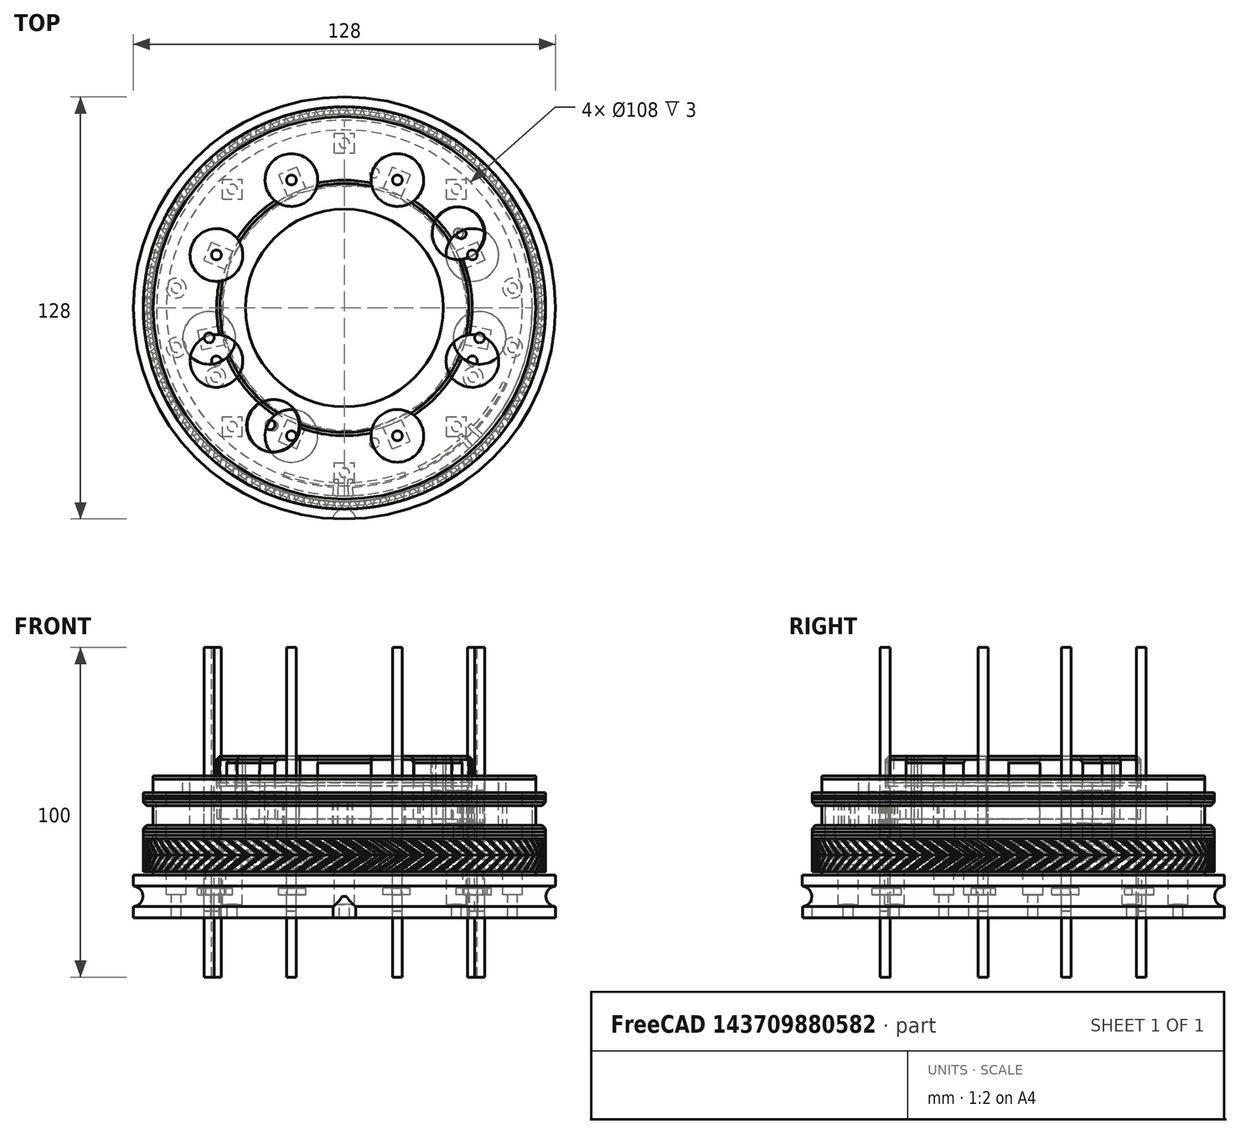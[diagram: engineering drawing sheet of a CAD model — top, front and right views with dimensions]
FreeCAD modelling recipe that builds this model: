
FCSTD DOCUMENT  (FreeCAD 0.19R24276 (Git))
Label: bazovina-part-F_pedestal_028
License: All rights reserved
LicenseURL: http://en.wikipedia.org/wiki/All_rights_reserved
objects: Part::Cylinder×215, Part::Cut×53, Part::Compound×50, Part::Box×36, Part::FeaturePython×26, Part::Chamfer×6, Mesh::Feature×4, Part::Torus×1
note: 387 computed .brp shape members not serialized (recipe doc carries the construction recipe); baked Part::Feature solids carry a one-line shape summary decoded from their .brp

FEATURE [Part::FeaturePython] Tube022  # WARN: FeaturePython — macro-defined, semantics opaque (R4)
  AttacherType = Attacher::AttachEngine3D
  Height = 19
  InnerRadius = 30
  OuterRadius = 58
  Placement = pos=(0,0,42) rot=(0,0,1;0rad)
FEATURE [Part::Cylinder] Cylinder433  label="Válec433"
  Angle = 360
  AttacherType = Attacher::AttachEngine3D
  Height = 18
  Placement = pos=(34.6278,22.6371,43.6023) rot=(-0.009819,-0.0017,0.99995;2.52972rad)
  Radius = 8
FEATURE [Part::Cylinder] Cylinder434  label="Válec434"
  Angle = 360
  AttacherType = Attacher::AttachEngine3D
  Height = 100
  Placement = pos=(16.0727,38.8029,0) rot=(0,0,1;3.14159rad)
  Radius = 1.5
FEATURE [Part::Cylinder] Cylinder435  label="Válec435"
  Angle = 360
  AttacherType = Attacher::AttachEngine3D
  Height = 18
  Placement = pos=(16.0725,38.7989,43) rot=(0,0,1;3.14159rad)
  Radius = 8
FEATURE [Part::Cylinder] Cylinder430  label="Válec430"
  Angle = 360
  AttacherType = Attacher::AttachEngine3D
  Height = 100
  Placement = pos=(38.8029,-16.0727,0) rot=(0,0,1;1.5708rad)
  Radius = 1.5
FEATURE [Part::Cylinder] Cylinder428  label="Válec428"
  Angle = 360
  AttacherType = Attacher::AttachEngine3D
  Height = 100
  Placement = pos=(16.0727,-38.8029,0) rot=(0,0,1;0.785398rad)
  Radius = 1.5
FEATURE [Part::Cylinder] Cylinder429  label="Válec429"
  Angle = 360
  AttacherType = Attacher::AttachEngine3D
  Height = 18
  Placement = pos=(16.07,-38.8,43) rot=(0,0,1;0.785398rad)
  Radius = 8
FEATURE [Part::Cylinder] Cylinder432  label="Válec432"
  Angle = 360
  AttacherType = Attacher::AttachEngine3D
  Height = 100
  Placement = pos=(35.44,22.5307,0.610113) rot=(-0.009819,-0.0017,0.99995;2.52972rad)
  Radius = 1.5
FEATURE [Part::Cylinder] Cylinder436  label="Válec436"
  Angle = 360
  AttacherType = Attacher::AttachEngine3D
  Height = 100
  Placement = pos=(-16.0727,38.8029,0) rot=(0,0,1;3.92699rad)
  Radius = 1.5
FEATURE [Part::Cylinder] Cylinder431  label="Válec431"
  Angle = 360
  AttacherType = Attacher::AttachEngine3D
  Height = 18
  Placement = pos=(38.7989,-16.0725,43) rot=(0,0,1;1.5708rad)
  Radius = 8
FEATURE [Part::Cylinder] Cylinder443  label="Válec443"
  Angle = 360
  AttacherType = Attacher::AttachEngine3D
  Height = 18
  Placement = pos=(-21.7485,-35.6902,43.196) rot=(0.02393,0.106372,-0.994038;0.174533rad)
  Radius = 8
FEATURE [Part::Cylinder] Cylinder438  label="Válec438"
  Angle = 360
  AttacherType = Attacher::AttachEngine3D
  Height = 100
  Placement = pos=(-38.8029,16.0727,0) rot=(0,0,-1;1.5708rad)
  Radius = 1.5
FEATURE [Part::Cylinder] Cylinder441  label="Válec441"
  Angle = 360
  AttacherType = Attacher::AttachEngine3D
  Height = 18
  Placement = pos=(-38.8,-16.07,43) rot=(0,0,-1;0.785398rad)
  Radius = 8
FEATURE [Part::Cylinder] Cylinder440  label="Válec440"
  Angle = 360
  AttacherType = Attacher::AttachEngine3D
  Height = 100
  Placement = pos=(-38.8029,-16.0727,0) rot=(0,0,-1;0.785398rad)
  Radius = 1.5
FEATURE [Part::Cylinder] Cylinder439  label="Válec439"
  Angle = 360
  AttacherType = Attacher::AttachEngine3D
  Height = 18
  Placement = pos=(-38.7989,16.0725,43) rot=(0,0,-1;1.5708rad)
  Radius = 8
FEATURE [Part::Cylinder] Cylinder442  label="Válec442"
  Angle = 360
  AttacherType = Attacher::AttachEngine3D
  Height = 100
  Placement = pos=(-22.5281,-35.4464,0.203785) rot=(0.02393,0.106372,-0.994038;0.174533rad)
  Radius = 1.5
FEATURE [Part::Compound] Compound321
  Links = -> [Cylinder428,Cylinder430,Cylinder432,Cylinder434,Cylinder436,Cylinder438,Cylinder440,Cylinder442]
FEATURE [Part::Cylinder] Cylinder437  label="Válec437"
  Angle = 360
  AttacherType = Attacher::AttachEngine3D
  Height = 18
  Placement = pos=(-16.07,38.8,43) rot=(0,0,1;3.92699rad)
  Radius = 8
FEATURE [Part::Compound] Compound323
  Links = -> [Cylinder441,Cylinder439,Cylinder437,Cylinder435,Cylinder433,Cylinder431,Cylinder429,Cylinder443]
  Placement = pos=(0,0,3) rot=(0,0,1;0rad)
FEATURE [Part::Cut] Cut169
  Base = -> Tube022
  Tool = -> Compound323
FEATURE [Part::Compound] Compound324
  Links = -> [Cut169]
FEATURE [Part::Cut] Cut170  label="bazovina-part-F_dirovina"
  Base = -> Compound324
  Tool = -> Compound321
FEATURE [Part::Cylinder] Cylinder444  label="Válec444"
  Angle = 360
  AttacherType = Attacher::AttachEngine3D
  Height = 25
  Placement = pos=(-21.7485,-35.6902,43.196) rot=(0.02393,0.106372,-0.994038;0.174533rad)
  Radius = 8
FEATURE [Part::Cylinder] Cylinder445  label="Válec445"
  Angle = 360
  AttacherType = Attacher::AttachEngine3D
  Height = 25
  Placement = pos=(-38.8,-16.07,43) rot=(0,0,-1;0.785398rad)
  Radius = 8
FEATURE [Part::Cylinder] Cylinder446  label="Válec446"
  Angle = 360
  AttacherType = Attacher::AttachEngine3D
  Height = 25
  Placement = pos=(-38.7989,16.0725,43) rot=(0,0,-1;1.5708rad)
  Radius = 8
FEATURE [Part::Cylinder] Cylinder447  label="Válec447"
  Angle = 360
  AttacherType = Attacher::AttachEngine3D
  Height = 25
  Placement = pos=(-16.07,38.8,43) rot=(0,0,1;3.92699rad)
  Radius = 8
FEATURE [Part::Cylinder] Cylinder448  label="Válec448"
  Angle = 360
  AttacherType = Attacher::AttachEngine3D
  Height = 25
  Placement = pos=(16.0725,38.7989,43) rot=(0,0,1;3.14159rad)
  Radius = 8
FEATURE [Part::Cylinder] Cylinder449  label="Válec449"
  Angle = 360
  AttacherType = Attacher::AttachEngine3D
  Height = 25
  Placement = pos=(34.6278,22.6371,43.6023) rot=(-0.009819,-0.0017,0.99995;2.52972rad)
  Radius = 8
FEATURE [Part::Cylinder] Cylinder450  label="Válec450"
  Angle = 360
  AttacherType = Attacher::AttachEngine3D
  Height = 25
  Placement = pos=(38.7989,-16.0725,43) rot=(0,0,1;1.5708rad)
  Radius = 8
FEATURE [Part::Cylinder] Cylinder451  label="Válec451"
  Angle = 360
  AttacherType = Attacher::AttachEngine3D
  Height = 25
  Placement = pos=(16.07,-38.8,43) rot=(0,0,1;0.785398rad)
  Radius = 8
FEATURE [Part::Compound] Compound325
  Links = -> [Cylinder445,Cylinder446,Cylinder447,Cylinder448,Cylinder449,Cylinder450,Cylinder451,Cylinder444]
  Placement = pos=(0,0,3) rot=(0,0,1;0rad)
FEATURE [Part::FeaturePython] Tube023  # WARN: FeaturePython — macro-defined, semantics opaque (R4)
  AttacherType = Attacher::AttachEngine3D
  Height = 18
  InnerRadius = 30
  OuterRadius = 38.65
  Placement = pos=(0,0,48) rot=(0,0,1;0rad)
FEATURE [Part::Cut] Cut
  Base = -> Tube023
  Tool = -> Compound325
FEATURE [Part::Compound] Compound  label="bazovina_part-F_pedestal-axial"
  Links = -> [Cut170,Cut]
FEATURE [Part::Cylinder] Cylinder290  label="Válec290"
  Angle = 360
  AttacherType = Attacher::AttachEngine3D
  Height = 20
  Placement = pos=(0,0,91) rot=(0,0,1;0rad)
  Radius = 38
FEATURE [Part::Cylinder] Cylinder289  label="Válec289"
  Angle = 360
  AttacherType = Attacher::AttachEngine3D
  Height = 20
  Placement = pos=(0,0,91) rot=(0,0,1;0rad)
  Radius = 38
FEATURE [Part::Cylinder] Cylinder461  label="Válec461"
  Angle = 360
  AttacherType = Attacher::AttachEngine3D
  Height = 100
  Placement = pos=(38.8029,-16.0727,0) rot=(0,0,1;1.5708rad)
  Radius = 1.5
FEATURE [Part::FeaturePython] wormgear023  # WARN: FeaturePython — macro-defined, semantics opaque (R4)
  AttacherType = Attacher::AttachEngine3D
  Placement = pos=(0,0,95) rot=(0,0,1;0.032289rad)
  beta = 33.6901
  clearance = 0.25
  diameter = 120
  head = 0
  height = 5
  module = 1
  pressure_angle = 20
  reverse_pitch = false
  teeth = 80
  version = 0.0.3
FEATURE [Part::Cut] Cut127
  Base = -> wormgear023
  Placement = pos=(0,0,-63) rot=(0,0,1;0rad)
  Tool = -> Cylinder290
FEATURE [Part::FeaturePython] wormgear022  # WARN: FeaturePython — macro-defined, semantics opaque (R4)
  AttacherType = Attacher::AttachEngine3D
  Placement = pos=(0,0,100) rot=(0,0,1;0rad)
  beta = 33.6901
  clearance = 0.25
  diameter = 120
  head = 0
  height = 5
  module = 1
  pressure_angle = 20
  reverse_pitch = true
  teeth = 80
  version = 0.0.3
FEATURE [Part::Cut] Cut128
  Base = -> wormgear022
  Placement = pos=(0,0,-63) rot=(0,0,1;0rad)
  Tool = -> Cylinder289
FEATURE [Part::Cylinder] Cylinder454  label="Válec454"
  Angle = 360
  AttacherType = Attacher::AttachEngine3D
  Height = 100
  Placement = pos=(38.8029,16.0727,0) rot=(0,0,1;2.35619rad)
  Radius = 1.5
FEATURE [Part::Cylinder] Cylinder455  label="Válec455"
  Angle = 360
  AttacherType = Attacher::AttachEngine3D
  Height = 100
  Placement = pos=(9.09046,41.0044,0) rot=(0,0,1;3.31613rad)
  Radius = 1.5
FEATURE [Part::Cylinder] Cylinder453  label="Válec453"
  Angle = 360
  AttacherType = Attacher::AttachEngine3D
  Height = 100
  Placement = pos=(38.8029,-16.0727,0) rot=(0,0,1;1.5708rad)
  Radius = 1.5
FEATURE [Part::Cylinder] Cylinder452  label="Válec452"
  Angle = 360
  AttacherType = Attacher::AttachEngine3D
  Height = 100
  Placement = pos=(9.09046,-41.0044,0) rot=(0,0,1;0.610865rad)
  Radius = 1.5
FEATURE [Part::Cylinder] Cylinder458  label="Válec458"
  Angle = 360
  AttacherType = Attacher::AttachEngine3D
  Height = 100
  Placement = pos=(-38.8029,-16.0727,0) rot=(0,0,-1;0.785398rad)
  Radius = 1.5
FEATURE [Part::Cylinder] Cylinder463  label="Válec463"
  Angle = 360
  AttacherType = Attacher::AttachEngine3D
  Height = 100
  Placement = pos=(9.09046,41.0044,0) rot=(0,0,1;3.31613rad)
  Radius = 1.5
FEATURE [Part::Cylinder] Cylinder456  label="Válec456"
  Angle = 360
  AttacherType = Attacher::AttachEngine3D
  Height = 100
  Placement = pos=(-16.0727,38.8029,0) rot=(0,0,1;3.92699rad)
  Radius = 1.5
FEATURE [Part::Cylinder] Cylinder459  label="Válec459"
  Angle = 360
  AttacherType = Attacher::AttachEngine3D
  Height = 100
  Placement = pos=(-16.0727,-38.8029,0) rot=(0,0,1;0rad)
  Radius = 1.5
FEATURE [Part::Cylinder] Cylinder465  label="Válec465"
  Angle = 360
  AttacherType = Attacher::AttachEngine3D
  Height = 100
  Placement = pos=(-38.8029,16.0727,0) rot=(0,0,-1;1.5708rad)
  Radius = 1.5
FEATURE [Part::Cylinder] Cylinder466  label="Válec466"
  Angle = 360
  AttacherType = Attacher::AttachEngine3D
  Height = 100
  Placement = pos=(-38.8029,-16.0727,0) rot=(0,0,-1;0.785398rad)
  Radius = 1.5
FEATURE [Part::Cylinder] Cylinder460  label="Válec460"
  Angle = 360
  AttacherType = Attacher::AttachEngine3D
  Height = 100
  Placement = pos=(9.09046,-41.0044,0) rot=(0,0,1;0.610865rad)
  Radius = 1.5
FEATURE [Part::Cylinder] Cylinder457  label="Válec457"
  Angle = 360
  AttacherType = Attacher::AttachEngine3D
  Height = 100
  Placement = pos=(-38.8029,16.0727,0) rot=(0,0,-1;1.5708rad)
  Radius = 1.5
FEATURE [Part::Compound] Compound326
  Links = -> [Cylinder452,Cylinder453,Cylinder454,Cylinder455,Cylinder456,Cylinder457,Cylinder458,Cylinder459]
FEATURE [Part::Cut] Cut171
  Base = -> Cut128
  Tool = -> Compound326
FEATURE [Part::Cylinder] Cylinder464  label="Válec464"
  Angle = 360
  AttacherType = Attacher::AttachEngine3D
  Height = 100
  Placement = pos=(-16.0727,38.8029,0) rot=(0,0,1;3.92699rad)
  Radius = 1.5
FEATURE [Part::Cylinder] Cylinder462  label="Válec462"
  Angle = 360
  AttacherType = Attacher::AttachEngine3D
  Height = 100
  Placement = pos=(38.8029,16.0727,0) rot=(0,0,1;2.35619rad)
  Radius = 1.5
FEATURE [Part::Cylinder] Cylinder467  label="Válec467"
  Angle = 360
  AttacherType = Attacher::AttachEngine3D
  Height = 100
  Placement = pos=(-16.0727,-38.8029,0) rot=(0,0,1;0rad)
  Radius = 1.5
FEATURE [Part::Compound] Compound327
  Links = -> [Cylinder460,Cylinder461,Cylinder462,Cylinder463,Cylinder464,Cylinder465,Cylinder466,Cylinder467]
FEATURE [Part::Cut] Cut172
  Base = -> Cut127
  Tool = -> Compound327
FEATURE [Part::Compound] Compound335  label="bazovina-part-D_ozubo"
  Links = -> [Cut171,Cut172]
FEATURE [Part::FeaturePython] Tube024  # WARN: FeaturePython — macro-defined, semantics opaque (R4)
  AttacherType = Attacher::AttachEngine3D
  Height = 3
  InnerRadius = 54
  OuterRadius = 61
  Placement = pos=(0,0,42) rot=(0,0,1;0rad)
FEATURE [Part::Chamfer] Chamfer
  Base = -> Tube024
  Edges = 1 edges r=1: [Edge1]
FEATURE [Part::FeaturePython] Tube025  # WARN: FeaturePython — macro-defined, semantics opaque (R4)
  AttacherType = Attacher::AttachEngine3D
  Height = 10
  InnerRadius = 30
  OuterRadius = 58
  Placement = pos=(0,0,42) rot=(0,0,1;0rad)
FEATURE [Part::Cylinder] Cylinder468  label="Válec468"
  Angle = 360
  AttacherType = Attacher::AttachEngine3D
  Height = 18
  Placement = pos=(-38.7989,16.0725,43) rot=(0,0,-1;1.5708rad)
  Radius = 8
FEATURE [Part::Cylinder] Cylinder469  label="Válec469"
  Angle = 360
  AttacherType = Attacher::AttachEngine3D
  Height = 100
  Placement = pos=(38.8029,-16.0727,0) rot=(0,0,1;1.5708rad)
  Radius = 1.5
FEATURE [Part::Cylinder] Cylinder470  label="Válec470"
  Angle = 360
  AttacherType = Attacher::AttachEngine3D
  Height = 100
  Placement = pos=(-38.8029,16.0727,0) rot=(0,0,-1;1.5708rad)
  Radius = 1.5
FEATURE [Part::Cylinder] Cylinder471  label="Válec471"
  Angle = 360
  AttacherType = Attacher::AttachEngine3D
  Height = 100
  Placement = pos=(16.0727,-38.8029,0) rot=(0,0,1;0.785398rad)
  Radius = 1.5
FEATURE [Part::Cylinder] Cylinder472  label="Válec472"
  Angle = 360
  AttacherType = Attacher::AttachEngine3D
  Height = 100
  Placement = pos=(35.44,22.5307,0.610113) rot=(-0.009819,-0.0017,0.99995;2.52972rad)
  Radius = 1.5
FEATURE [Part::Cylinder] Cylinder473  label="Válec473"
  Angle = 360
  AttacherType = Attacher::AttachEngine3D
  Height = 18
  Placement = pos=(-21.7485,-35.6902,43.196) rot=(0.02393,0.106372,-0.994038;0.174533rad)
  Radius = 8
FEATURE [Part::Cylinder] Cylinder474  label="Válec474"
  Angle = 360
  AttacherType = Attacher::AttachEngine3D
  Height = 18
  Placement = pos=(38.7989,-16.0725,43) rot=(0,0,1;1.5708rad)
  Radius = 8
FEATURE [Part::Cylinder] Cylinder475  label="Válec475"
  Angle = 360
  AttacherType = Attacher::AttachEngine3D
  Height = 100
  Placement = pos=(-38.8029,-16.0727,0) rot=(0,0,-1;0.785398rad)
  Radius = 1.5
FEATURE [Part::Cylinder] Cylinder476  label="Válec476"
  Angle = 360
  AttacherType = Attacher::AttachEngine3D
  Height = 100
  Placement = pos=(-16.0727,38.8029,0) rot=(0,0,1;3.92699rad)
  Radius = 1.5
FEATURE [Part::Cylinder] Cylinder477  label="Válec477"
  Angle = 360
  AttacherType = Attacher::AttachEngine3D
  Height = 18
  Placement = pos=(-38.8,-16.07,43) rot=(0,0,-1;0.785398rad)
  Radius = 8
FEATURE [Part::Cylinder] Cylinder478  label="Válec478"
  Angle = 360
  AttacherType = Attacher::AttachEngine3D
  Height = 18
  Placement = pos=(16.07,-38.8,43) rot=(0,0,1;0.785398rad)
  Radius = 8
FEATURE [Part::Cylinder] Cylinder479  label="Válec479"
  Angle = 360
  AttacherType = Attacher::AttachEngine3D
  Height = 100
  Placement = pos=(-22.5281,-35.4464,0.203785) rot=(0.02393,0.106372,-0.994038;0.174533rad)
  Radius = 1.5
FEATURE [Part::Cylinder] Cylinder480  label="Válec480"
  Angle = 360
  AttacherType = Attacher::AttachEngine3D
  Height = 18
  Placement = pos=(-16.07,38.8,43) rot=(0,0,1;3.92699rad)
  Radius = 8
FEATURE [Part::Cylinder] Cylinder481  label="Válec481"
  Angle = 360
  AttacherType = Attacher::AttachEngine3D
  Height = 100
  Placement = pos=(16.0727,38.8029,0) rot=(0,0,1;3.14159rad)
  Radius = 1.5
FEATURE [Part::Compound] Compound338
  Links = -> [Cylinder471,Cylinder469,Cylinder472,Cylinder481,Cylinder476,Cylinder470,Cylinder475,Cylinder479]
FEATURE [Part::Cylinder] Cylinder482  label="Válec482"
  Angle = 360
  AttacherType = Attacher::AttachEngine3D
  Height = 18
  Placement = pos=(34.6278,22.6371,43.6023) rot=(-0.009819,-0.0017,0.99995;2.52972rad)
  Radius = 8
FEATURE [Part::Cylinder] Cylinder483  label="Válec483"
  Angle = 360
  AttacherType = Attacher::AttachEngine3D
  Height = 18
  Placement = pos=(16.0725,38.7989,43) rot=(0,0,1;3.14159rad)
  Radius = 8
FEATURE [Part::Compound] Compound336
  Links = -> [Cylinder477,Cylinder468,Cylinder480,Cylinder483,Cylinder482,Cylinder474,Cylinder478,Cylinder473]
  Placement = pos=(0,0,3) rot=(0,0,1;0rad)
FEATURE [Part::Cut] Cut173
  Base = -> Tube025
  Tool = -> Compound336
FEATURE [Part::Compound] Compound337
  Links = -> [Cut173]
FEATURE [Part::Cut] Cut174  label="bazovina-part-F_dirovina001"
  Base = -> Compound337
  Tool = -> Compound338
FEATURE [Part::Cylinder] Cylinder484  label="Válec484"
  Angle = 360
  AttacherType = Attacher::AttachEngine3D
  Height = 100
  Placement = pos=(38.8029,-16.0727,0) rot=(0,0,1;1.5708rad)
  Radius = 1.5
FEATURE [Part::Cylinder] Cylinder485  label="Válec485"
  Angle = 360
  AttacherType = Attacher::AttachEngine3D
  Height = 100
  Placement = pos=(16.0727,-38.8029,0) rot=(0,0,1;0.785398rad)
  Radius = 1.5
FEATURE [Part::Cylinder] Cylinder486  label="Válec486"
  Angle = 360
  AttacherType = Attacher::AttachEngine3D
  Height = 100
  Placement = pos=(35.44,22.5307,0.610113) rot=(-0.009819,-0.0017,0.99995;2.52972rad)
  Radius = 1.5
FEATURE [Part::Cylinder] Cylinder487  label="Válec487"
  Angle = 360
  AttacherType = Attacher::AttachEngine3D
  Height = 100
  Placement = pos=(-38.8029,16.0727,0) rot=(0,0,-1;1.5708rad)
  Radius = 1.5
FEATURE [Part::Cylinder] Cylinder488  label="Válec488"
  Angle = 360
  AttacherType = Attacher::AttachEngine3D
  Height = 100
  Placement = pos=(-38.8029,-16.0727,0) rot=(0,0,-1;0.785398rad)
  Radius = 1.5
FEATURE [Part::Cylinder] Cylinder489  label="Válec489"
  Angle = 360
  AttacherType = Attacher::AttachEngine3D
  Height = 100
  Placement = pos=(16.0727,38.8029,0) rot=(0,0,1;3.14159rad)
  Radius = 1.5
FEATURE [Part::Cylinder] Cylinder490  label="Válec490"
  Angle = 360
  AttacherType = Attacher::AttachEngine3D
  Height = 100
  Placement = pos=(-16.0727,38.8029,0) rot=(0,0,1;3.92699rad)
  Radius = 1.5
FEATURE [Part::Cylinder] Cylinder491  label="Válec491"
  Angle = 360
  AttacherType = Attacher::AttachEngine3D
  Height = 100
  Placement = pos=(-22.5281,-35.4464,0.203785) rot=(0.02393,0.106372,-0.994038;0.174533rad)
  Radius = 1.5
FEATURE [Part::Compound] Compound339
  Links = -> [Cylinder485,Cylinder484,Cylinder486,Cylinder489,Cylinder490,Cylinder487,Cylinder488,Cylinder491]
FEATURE [Part::FeaturePython] Tube026  # WARN: FeaturePython — macro-defined, semantics opaque (R4)
  AttacherType = Attacher::AttachEngine3D
  Height = 10
  InnerRadius = 30
  OuterRadius = 57
  Placement = pos=(0,0,42) rot=(0,0,1;0rad)
FEATURE [Part::Cut] Cut175
  Base = -> Tube026
  Tool = -> Compound339
FEATURE [Part::Box] Box298  label="Krychle298"
  AttacherType = Attacher::AttachEngine3D
  Height = 7
  Length = 60
  Placement = pos=(0,0,-22) rot=(0,0,-1;0.349066rad)
  Width = 60
FEATURE [Part::Box] Box300  label="Krychle300"
  AttacherType = Attacher::AttachEngine3D
  Height = 7
  Length = 120
  Placement = pos=(-60,-60,-22) rot=(0,0,-1;0rad)
  Width = 60
FEATURE [Part::Box] Box299  label="Krychle299"
  AttacherType = Attacher::AttachEngine3D
  Height = 7
  Length = 60
  Placement = pos=(-56.3816,-20.5212,-22) rot=(0,0,1;0.349066rad)
  Width = 60
FEATURE [Part::FeaturePython] Tube071  # WARN: FeaturePython — macro-defined, semantics opaque (R4)
  AttacherType = Attacher::AttachEngine3D
  Height = 7
  InnerRadius = 53
  OuterRadius = 54.4
  Placement = pos=(0,0,-22) rot=(0,0,1;0rad)
FEATURE [Part::Cut] Cut308
  Base = -> Tube071
  Tool = -> Box300
FEATURE [Part::FeaturePython] Tube074  # WARN: FeaturePython — macro-defined, semantics opaque (R4)
  AttacherType = Attacher::AttachEngine3D
  Height = 7
  InnerRadius = 53
  OuterRadius = 54.4
  Placement = pos=(0,0,-22) rot=(0,0,1;0rad)
FEATURE [Part::Compound] Compound690
  Links = -> [Box298,Box299]
FEATURE [Part::Cut] Cut309
  Base = -> Cut308
  Placement = pos=(0,0,-7) rot=(0,0,1;0rad)
  Tool = -> Compound690
FEATURE [Part::Box] Box304  label="Krychle304"
  AttacherType = Attacher::AttachEngine3D
  Height = 7
  Length = 120
  Placement = pos=(-60,-60,-22) rot=(0,0,-1;0rad)
  Width = 60
FEATURE [Part::Cut] Cut312
  Base = -> Tube074
  Tool = -> Box304
FEATURE [Part::Box] Box306  label="Krychle306"
  AttacherType = Attacher::AttachEngine3D
  Height = 7
  Length = 60
  Placement = pos=(-59.9909,-1.04714,-22) rot=(0,0,1;0.017453rad)
  Width = 60
FEATURE [Part::Box] Box305  label="Krychle305"
  AttacherType = Attacher::AttachEngine3D
  Height = 7
  Length = 60
  Placement = pos=(0,0,-22) rot=(0,0,-1;0.034907rad)
  Width = 60
FEATURE [Part::Compound] Compound694
  Links = -> [Box305,Box306]
FEATURE [Part::Cut] Cut313
  Base = -> Cut312
  Placement = pos=(0,0,-7) rot=(0,0,1;0rad)
  Tool = -> Compound694
FEATURE [Part::Cut] Cut314
  Base = -> Cut309
  Placement = pos=(0,0,74) rot=(0,0,1;3.14159rad)
  Tool = -> Cut313
FEATURE [Part::Box] Box301  label="Krychle301"
  AttacherType = Attacher::AttachEngine3D
  Height = 7
  Length = 1.4
  Placement = pos=(0,0,-22) rot=(0,0,-1;0.034907rad)
  Width = 60
FEATURE [Part::Box] Box302  label="Krychle302"
  AttacherType = Attacher::AttachEngine3D
  Height = 7
  Length = 1.4
  Placement = pos=(0,0,-22) rot=(0,0,1;0.047124rad)
  Width = 60
FEATURE [Part::Cylinder] Cylinder689  label="Válec689"
  Angle = 360
  AttacherType = Attacher::AttachEngine3D
  Height = 7
  Placement = pos=(0,0,-22) rot=(0,0,1;0rad)
  Radius = 52
FEATURE [Part::Compound] Compound691
  Links = -> [Box301,Box302]
FEATURE [Part::Cut] Cut310
  Base = -> Compound691
  Placement = pos=(0,0,67) rot=(0,0,1;3.13985rad)
  Tool = -> Cylinder689
FEATURE [Part::Cut] Cut315
  Base = -> Cut175
  Tool = -> Cut314
FEATURE [Part::Cut] Cut316
  Base = -> Cut315
  Tool = -> Cut310
FEATURE [Part::Compound] Compound695  label="bazovina_part-F_pedestal-axial-A-belt-old"
  Links = -> [Chamfer,Cut316]
  Placement = pos=(0,0,1) rot=(0,0,1;0rad)
FEATURE [Part::Cylinder] Cylinder690  label="Válec690"
  Angle = 360
  AttacherType = Attacher::AttachEngine3D
  Height = 25
  Placement = pos=(-21.7485,-35.6902,43.196) rot=(0.02393,0.106372,-0.994038;0.174533rad)
  Radius = 8
FEATURE [Part::Cylinder] Cylinder691  label="Válec691"
  Angle = 360
  AttacherType = Attacher::AttachEngine3D
  Height = 25
  Placement = pos=(-38.8,-16.07,43) rot=(0,0,-1;0.785398rad)
  Radius = 8
FEATURE [Part::Cylinder] Cylinder692  label="Válec692"
  Angle = 360
  AttacherType = Attacher::AttachEngine3D
  Height = 25
  Placement = pos=(-38.7989,16.0725,43) rot=(0,0,-1;1.5708rad)
  Radius = 8
FEATURE [Part::Cylinder] Cylinder693  label="Válec693"
  Angle = 360
  AttacherType = Attacher::AttachEngine3D
  Height = 25
  Placement = pos=(-16.07,38.8,43) rot=(0,0,1;3.92699rad)
  Radius = 8
FEATURE [Part::Cylinder] Cylinder694  label="Válec694"
  Angle = 360
  AttacherType = Attacher::AttachEngine3D
  Height = 25
  Placement = pos=(34.63,22.64,43.6) rot=(0,0,1;2.53073rad)
  Radius = 8
FEATURE [Part::Cylinder] Cylinder695  label="Válec695"
  Angle = 360
  AttacherType = Attacher::AttachEngine3D
  Height = 25
  Placement = pos=(16.0725,38.7989,43) rot=(0,0,1;3.14159rad)
  Radius = 8
FEATURE [Part::Cylinder] Cylinder696  label="Válec696"
  Angle = 360
  AttacherType = Attacher::AttachEngine3D
  Height = 25
  Placement = pos=(38.7989,-16.0725,43) rot=(0,0,1;1.5708rad)
  Radius = 8
FEATURE [Part::Cylinder] Cylinder697  label="Válec697"
  Angle = 360
  AttacherType = Attacher::AttachEngine3D
  Height = 25
  Placement = pos=(16.07,-38.8,43) rot=(0,0,1;0.785398rad)
  Radius = 8
FEATURE [Part::Compound] Compound696
  Links = -> [Cylinder691,Cylinder692,Cylinder693,Cylinder695,Cylinder694,Cylinder696,Cylinder697,Cylinder690]
  Placement = pos=(0,0,3) rot=(0,0,1;0rad)
FEATURE [Part::FeaturePython] Tube075  # WARN: FeaturePython — macro-defined, semantics opaque (R4)
  AttacherType = Attacher::AttachEngine3D
  Height = 8
  InnerRadius = 30
  OuterRadius = 38.75
  Placement = pos=(0,0,58) rot=(0,0,1;0rad)
FEATURE [Part::Cut] Cut317
  Base = -> Tube075
  Tool = -> Compound696
FEATURE [Part::Cylinder] Cylinder698  label="Válec698"
  Angle = 360
  AttacherType = Attacher::AttachEngine3D
  Height = 18
  Placement = pos=(34.63,22.64,43.6) rot=(0,0,1;2.53073rad)
  Radius = 8
FEATURE [Part::Cylinder] Cylinder699  label="Válec699"
  Angle = 360
  AttacherType = Attacher::AttachEngine3D
  Height = 100
  Placement = pos=(16.0727,38.8029,0) rot=(0,0,1;3.14159rad)
  Radius = 1.5
FEATURE [Part::Cylinder] Cylinder700  label="Válec700"
  Angle = 360
  AttacherType = Attacher::AttachEngine3D
  Height = 18
  Placement = pos=(16.0725,38.7989,43) rot=(0,0,1;3.14159rad)
  Radius = 8
FEATURE [Part::FeaturePython] Tube076  # WARN: FeaturePython — macro-defined, semantics opaque (R4)
  AttacherType = Attacher::AttachEngine3D
  Height = 8
  InnerRadius = 30
  OuterRadius = 58
  Placement = pos=(0,0,52) rot=(0,0,1;0rad)
FEATURE [Part::Cylinder] Cylinder701  label="Válec701"
  Angle = 360
  AttacherType = Attacher::AttachEngine3D
  Height = 100
  Placement = pos=(-22.53,-35.45,0.2) rot=(0,0,1;0.174533rad)
  Radius = 1.5
FEATURE [Part::Cylinder] Cylinder702  label="Válec702"
  Angle = 360
  AttacherType = Attacher::AttachEngine3D
  Height = 100
  Placement = pos=(38.8029,-16.0727,0) rot=(0,0,1;1.5708rad)
  Radius = 1.5
FEATURE [Part::Cylinder] Cylinder703  label="Válec703"
  Angle = 360
  AttacherType = Attacher::AttachEngine3D
  Height = 18
  Placement = pos=(-38.8,-16.07,43) rot=(0,0,-1;0.785398rad)
  Radius = 8
FEATURE [Part::Cylinder] Cylinder704  label="Válec704"
  Angle = 360
  AttacherType = Attacher::AttachEngine3D
  Height = 18
  Placement = pos=(-16.07,38.8,43) rot=(0,0,1;3.92699rad)
  Radius = 8
FEATURE [Part::Cylinder] Cylinder705  label="Válec705"
  Angle = 360
  AttacherType = Attacher::AttachEngine3D
  Height = 18
  Placement = pos=(-21.7485,-35.6902,43.196) rot=(0.02393,0.106372,-0.994038;0.174533rad)
  Radius = 8
FEATURE [Part::Cylinder] Cylinder706  label="Válec706"
  Angle = 360
  AttacherType = Attacher::AttachEngine3D
  Height = 100
  Placement = pos=(16.0727,-38.8029,0) rot=(0,0,1;0.785398rad)
  Radius = 1.5
FEATURE [Part::Cylinder] Cylinder707  label="Válec707"
  Angle = 360
  AttacherType = Attacher::AttachEngine3D
  Height = 100
  Placement = pos=(-16.0727,38.8029,0) rot=(0,0,1;3.92699rad)
  Radius = 1.5
FEATURE [Part::Cylinder] Cylinder708  label="Válec708"
  Angle = 360
  AttacherType = Attacher::AttachEngine3D
  Height = 100
  Placement = pos=(35.44,22.53,0.61) rot=(0,0,1;2.53073rad)
  Radius = 1.5
FEATURE [Part::Cylinder] Cylinder709  label="Válec709"
  Angle = 360
  AttacherType = Attacher::AttachEngine3D
  Height = 18
  Placement = pos=(16.07,-38.8,43) rot=(0,0,1;0.785398rad)
  Radius = 8
FEATURE [Part::Cylinder] Cylinder710  label="Válec710"
  Angle = 360
  AttacherType = Attacher::AttachEngine3D
  Height = 100
  Placement = pos=(-38.8029,-16.0727,0) rot=(0,0,-1;0.785398rad)
  Radius = 1.5
FEATURE [Part::Cylinder] Cylinder711  label="Válec711"
  Angle = 360
  AttacherType = Attacher::AttachEngine3D
  Height = 100
  Placement = pos=(-38.8029,16.0727,0) rot=(0,0,-1;1.5708rad)
  Radius = 1.5
FEATURE [Part::Compound] Compound697
  Links = -> [Cylinder706,Cylinder702,Cylinder708,Cylinder699,Cylinder707,Cylinder711,Cylinder710,Cylinder701]
FEATURE [Part::Cylinder] Cylinder712  label="Válec712"
  Angle = 360
  AttacherType = Attacher::AttachEngine3D
  Height = 18
  Placement = pos=(38.7989,-16.0725,43) rot=(0,0,1;1.5708rad)
  Radius = 8
FEATURE [Part::Cylinder] Cylinder713  label="Válec713"
  Angle = 360
  AttacherType = Attacher::AttachEngine3D
  Height = 18
  Placement = pos=(-38.7989,16.0725,43) rot=(0,0,-1;1.5708rad)
  Radius = 8
FEATURE [Part::Compound] Compound698
  Links = -> [Cylinder703,Cylinder713,Cylinder704,Cylinder700,Cylinder698,Cylinder712,Cylinder709,Cylinder705]
  Placement = pos=(0,0,12) rot=(0,0,1;0rad)
FEATURE [Part::Cut] Cut318
  Base = -> Tube076
  Tool = -> Compound698
FEATURE [Part::Compound] Compound699
  Links = -> [Cut318]
FEATURE [Part::Cut] Cut319  label="bazovina-part-F_dirovina002"
  Base = -> Compound699
  Tool = -> Compound697
FEATURE [Part::FeaturePython] Tube077  # WARN: FeaturePython — macro-defined, semantics opaque (R4)
  AttacherType = Attacher::AttachEngine3D
  Height = 3
  InnerRadius = 54
  OuterRadius = 61
  Placement = pos=(0,0,52) rot=(0,0,1;0rad)
FEATURE [Part::Chamfer] Chamfer001
  Base = -> Cut317
  Edges = 9 edges r=1: [Edge4,Edge5,Edge26,Edge28,Edge30,Edge32,Edge34,Edge36,Edge38]
FEATURE [Part::Chamfer] Chamfer002
  Base = -> Tube077
  Edges = 1 edges r=1: [Edge3]
FEATURE [Part::Compound] Compound700  label="bazovina_part-F_pedestal-axial-B_old"
  Links = -> [Chamfer001,Cut319,Chamfer002]
  Placement = pos=(0,0,1) rot=(0,0,1;0rad)
FEATURE [Part::Cylinder] Cylinder714  label="Válec714"
  Angle = 360
  AttacherType = Attacher::AttachEngine3D
  Height = 100
  Placement = pos=(-22.5281,-35.4464,0.203785) rot=(0.02393,0.106372,-0.994038;0.174533rad)
  Radius = 1.5
FEATURE [Part::Cylinder] Cylinder715  label="Válec715"
  Angle = 360
  AttacherType = Attacher::AttachEngine3D
  Height = 100
  Placement = pos=(16.0727,38.8029,0) rot=(0,0,1;3.14159rad)
  Radius = 1.5
FEATURE [Part::Cylinder] Cylinder716  label="Válec716"
  Angle = 360
  AttacherType = Attacher::AttachEngine3D
  Height = 100
  Placement = pos=(38.8029,-16.0727,0) rot=(0,0,1;1.5708rad)
  Radius = 1.5
FEATURE [Part::Cylinder] Cylinder717  label="Válec717"
  Angle = 360
  AttacherType = Attacher::AttachEngine3D
  Height = 100
  Placement = pos=(-16.0727,38.8029,0) rot=(0,0,1;3.92699rad)
  Radius = 1.5
FEATURE [Part::Cylinder] Cylinder718  label="Válec718"
  Angle = 360
  AttacherType = Attacher::AttachEngine3D
  Height = 100
  Placement = pos=(16.0727,-38.8029,0) rot=(0,0,1;0.785398rad)
  Radius = 1.5
FEATURE [Part::Cylinder] Cylinder719  label="Válec719"
  Angle = 360
  AttacherType = Attacher::AttachEngine3D
  Height = 100
  Placement = pos=(-38.8029,-16.0727,0) rot=(0,0,-1;0.785398rad)
  Radius = 1.5
FEATURE [Part::Cylinder] Cylinder720  label="Válec720"
  Angle = 360
  AttacherType = Attacher::AttachEngine3D
  Height = 100
  Placement = pos=(35.44,22.5307,0.610113) rot=(-0.009819,-0.0017,0.99995;2.52972rad)
  Radius = 1.5
FEATURE [Part::Cylinder] Cylinder721  label="Válec721"
  Angle = 360
  AttacherType = Attacher::AttachEngine3D
  Height = 100
  Placement = pos=(-38.8029,16.0727,0) rot=(0,0,-1;1.5708rad)
  Radius = 1.5
FEATURE [Part::Compound] Compound701
  Links = -> [Cylinder718,Cylinder716,Cylinder720,Cylinder715,Cylinder717,Cylinder721,Cylinder719,Cylinder714]
FEATURE [Part::FeaturePython] Tube078  # WARN: FeaturePython — macro-defined, semantics opaque (R4)
  AttacherType = Attacher::AttachEngine3D
  Height = 1
  InnerRadius = 38
  OuterRadius = 58
  Placement = pos=(0,0,42) rot=(0,0,1;0rad)
FEATURE [Part::Cut] Cut320  label="bazovina_part-F_washer-old"
  Base = -> Tube078
  Tool = -> Compound701
FEATURE [Part::Cylinder] Cylinder371  label="Válec371"
  Angle = 360
  AttacherType = Attacher::AttachEngine3D
  Height = 50
  Placement = pos=(34,36,0) rot=(0,0,1;0rad)
  Radius = 1.5
FEATURE [Part::Cylinder] Cylinder372  label="Válec372"
  Angle = 360
  AttacherType = Attacher::AttachEngine3D
  Height = 50
  Placement = pos=(-34,-36,0) rot=(0,0,1;0rad)
  Radius = 1.5
FEATURE [Part::Cylinder] Cylinder288  label="Válec288"
  Angle = 360
  AttacherType = Attacher::AttachEngine3D
  Height = 20
  Placement = pos=(0,-64.5,4.5) rot=(0,0,1;0rad)
  Radius = 3.5
FEATURE [Part::Torus] Torus  label="Anuloid"
  Angle1 = -180
  Angle2 = 180
  Angle3 = 360
  AttacherType = Attacher::AttachEngine3D
  Placement = pos=(0,0,24.5) rot=(0,0,1;0rad)
  Radius1 = 64.2
  Radius2 = 3.1
FEATURE [Part::FeaturePython] Tube019  # WARN: FeaturePython — macro-defined, semantics opaque (R4)
  AttacherType = Attacher::AttachEngine3D
  Height = 13
  InnerRadius = 38
  OuterRadius = 64
  Placement = pos=(0,0,18) rot=(0,0,1;0rad)
FEATURE [Part::FeaturePython] Tube020  # WARN: FeaturePython — macro-defined, semantics opaque (R4)
  AttacherType = Attacher::AttachEngine3D
  Height = 1
  InnerRadius = 38
  OuterRadius = 58
  Placement = pos=(0,0,31) rot=(0,0,1;0rad)
FEATURE [Part::Cut] Cut129
  Base = -> Tube019
  Tool = -> Torus
FEATURE [Part::Cut] Cut130
  Base = -> Cut129
  Tool = -> Cylinder288
FEATURE [Part::Cylinder] Cylinder379  label="Válec379"
  Angle = 360
  AttacherType = Attacher::AttachEngine3D
  Height = 100
  Placement = pos=(51,-12,0) rot=(0,0,1;0rad)
  Radius = 1.5
FEATURE [Part::Cylinder] Cylinder408  label="Válec408"
  Angle = 360
  AttacherType = Attacher::AttachEngine3D
  Height = 7
  Placement = pos=(-51,-12,50) rot=(0,0,1;0rad)
  Radius = 3
FEATURE [Part::Box] Box149  label="Krychle149"
  AttacherType = Attacher::AttachEngine3D
  Height = 10
  Length = 6
  Placement = pos=(-37,33,40) rot=(0,0,1;0rad)
  Width = 6
FEATURE [Part::Cylinder] Cylinder375  label="Válec375"
  Angle = 360
  AttacherType = Attacher::AttachEngine3D
  Height = 50
  Placement = pos=(0,-50,0) rot=(0,0,1;0rad)
  Radius = 1.5
FEATURE [Part::Cylinder] Cylinder376  label="Válec376"
  Angle = 360
  AttacherType = Attacher::AttachEngine3D
  Height = 100
  Placement = pos=(-51,-12,0) rot=(0,0,1;0rad)
  Radius = 1.5
FEATURE [Part::Box] Box150  label="Krychle150"
  AttacherType = Attacher::AttachEngine3D
  Height = 10
  Length = 6
  Placement = pos=(31,-39,40) rot=(0,0,1;0rad)
  Width = 6
FEATURE [Part::Cylinder] Cylinder406  label="Válec406"
  Angle = 360
  AttacherType = Attacher::AttachEngine3D
  Height = 7
  Placement = pos=(-51,-12,50) rot=(0,0,1;0rad)
  Radius = 3
FEATURE [Part::Cylinder] Cylinder411  label="Válec411"
  Angle = 360
  AttacherType = Attacher::AttachEngine3D
  Height = 7
  Placement = pos=(51,-12,50) rot=(0,0,1;0rad)
  Radius = 3
FEATURE [Part::Cylinder] Cylinder405  label="Válec405"
  Angle = 360
  AttacherType = Attacher::AttachEngine3D
  Height = 7
  Placement = pos=(51,6,50) rot=(0,0,1;0rad)
  Radius = 3
FEATURE [Part::Cylinder] Cylinder373  label="Válec373"
  Angle = 360
  AttacherType = Attacher::AttachEngine3D
  Height = 50
  Placement = pos=(34,-36,0) rot=(0,0,1;0rad)
  Radius = 1.5
FEATURE [Part::Cylinder] Cylinder374  label="Válec374"
  Angle = 360
  AttacherType = Attacher::AttachEngine3D
  Height = 50
  Placement = pos=(0,50,0) rot=(0,0,1;0rad)
  Radius = 1.5
FEATURE [Part::Cylinder] Cylinder377  label="Válec377"
  Angle = 360
  AttacherType = Attacher::AttachEngine3D
  Height = 50
  Placement = pos=(51,6,0) rot=(0,0,1;0rad)
  Radius = 1.5
FEATURE [Part::Cylinder] Cylinder409  label="Válec409"
  Angle = 360
  AttacherType = Attacher::AttachEngine3D
  Height = 7
  Placement = pos=(51,6,50) rot=(0,0,1;0rad)
  Radius = 3
FEATURE [Part::Cylinder] Cylinder370  label="Válec370"
  Angle = 360
  AttacherType = Attacher::AttachEngine3D
  Height = 50
  Placement = pos=(-34,36,0) rot=(0,0,1;0rad)
  Radius = 1.5
FEATURE [Part::Cylinder] Cylinder404  label="Válec404"
  Angle = 360
  AttacherType = Attacher::AttachEngine3D
  Height = 7
  Placement = pos=(-51,6,50) rot=(0,0,1;0rad)
  Radius = 3
FEATURE [Part::Cylinder] Cylinder378  label="Válec378"
  Angle = 360
  AttacherType = Attacher::AttachEngine3D
  Height = 50
  Placement = pos=(-51,6,0) rot=(0,0,1;0rad)
  Radius = 1.5
FEATURE [Part::Compound] Compound308
  Links = -> [Cylinder370,Cylinder371,Cylinder372,Cylinder373,Cylinder374,Cylinder375,Cylinder376,Cylinder377,Cylinder378,Cylinder379]
FEATURE [Part::Cut] Cut160
  Base = -> Cut130
  Tool = -> Compound308
FEATURE [Part::Box] Box154  label="Krychle154"
  AttacherType = Attacher::AttachEngine3D
  Height = 10
  Length = 6
  Placement = pos=(-37,-39,40) rot=(0,0,1;0rad)
  Width = 6
FEATURE [Part::Box] Box153  label="Krychle153"
  AttacherType = Attacher::AttachEngine3D
  Height = 10
  Length = 6
  Placement = pos=(-37,33,40) rot=(0,0,1;0rad)
  Width = 6
FEATURE [Part::Box] Box157  label="Krychle157"
  AttacherType = Attacher::AttachEngine3D
  Height = 2
  Length = 6
  Placement = pos=(14.4491,-42.7226,25) rot=(0,0,1;0.392699rad)
  Width = 8
FEATURE [Part::Box] Box162  label="Krychle162"
  AttacherType = Attacher::AttachEngine3D
  Height = 2
  Length = 6
  Placement = pos=(-40.4265,19.9924,25) rot=(0,0,-1;1.96349rad)
  Width = 8
FEATURE [Part::Cylinder] Cylinder410  label="Válec410"
  Angle = 360
  AttacherType = Attacher::AttachEngine3D
  Height = 7
  Placement = pos=(-51,6,50) rot=(0,0,1;0rad)
  Radius = 3
FEATURE [Part::Compound] Compound313
  Links = -> [Cylinder408,Cylinder411,Cylinder409,Cylinder410]
  Placement = pos=(0,0,-25) rot=(0,0,1;0rad)
FEATURE [Part::Cut] Cut162
  Base = -> Cut160
  Tool = -> Compound313
FEATURE [Part::Box] Box146  label="Krychle146"
  AttacherType = Attacher::AttachEngine3D
  Height = 10
  Length = 6
  Placement = pos=(-3,-53,40) rot=(0,0,1;0rad)
  Width = 6
FEATURE [Part::Box] Box147  label="Krychle147"
  AttacherType = Attacher::AttachEngine3D
  Height = 10
  Length = 6
  Placement = pos=(-37,-39,40) rot=(0,0,1;0rad)
  Width = 6
FEATURE [Part::Box] Box145  label="Krychle145"
  AttacherType = Attacher::AttachEngine3D
  Height = 10
  Length = 6
  Placement = pos=(-3,47,40) rot=(0,0,1;0rad)
  Width = 6
FEATURE [Part::Cylinder] Cylinder407  label="Válec407"
  Angle = 360
  AttacherType = Attacher::AttachEngine3D
  Height = 7
  Placement = pos=(51,-12,50) rot=(0,0,1;0rad)
  Radius = 3
FEATURE [Part::Compound] Compound312
  Links = -> [Cylinder406,Cylinder407,Cylinder405,Cylinder404]
  Placement = pos=(0,0,-25) rot=(0,0,1;0rad)
FEATURE [Part::Cut] Cut161
  Base = -> Tube020
  Tool = -> Compound312
FEATURE [Part::Box] Box151  label="Krychle151"
  AttacherType = Attacher::AttachEngine3D
  Height = 10
  Length = 6
  Placement = pos=(-3,-53,40) rot=(0,0,1;0rad)
  Width = 6
FEATURE [Part::Box] Box148  label="Krychle148"
  AttacherType = Attacher::AttachEngine3D
  Height = 10
  Length = 6
  Placement = pos=(31,33,40) rot=(0,0,1;0rad)
  Width = 6
FEATURE [Part::Compound] Compound315
  Links = -> [Box145,Box147,Box146,Box148,Box149,Box150]
  Placement = pos=(0,0,-18) rot=(0,0,1;0rad)
FEATURE [Part::Cut] Cut164
  Base = -> Cut162
  Tool = -> Compound315
FEATURE [Part::Box] Box156  label="Krychle156"
  AttacherType = Attacher::AttachEngine3D
  Height = 10
  Length = 6
  Placement = pos=(31,-39,40) rot=(0,0,1;0rad)
  Width = 6
FEATURE [Part::Box] Box155  label="Krychle155"
  AttacherType = Attacher::AttachEngine3D
  Height = 10
  Length = 6
  Placement = pos=(31,33,40) rot=(0,0,1;0rad)
  Width = 6
FEATURE [Part::Box] Box158  label="Krychle158"
  AttacherType = Attacher::AttachEngine3D
  Height = 2
  Length = 6
  Placement = pos=(43.284,-12.6687,25) rot=(0,0,1;1.35263rad)
  Width = 8
FEATURE [Part::Box] Box159  label="Krychle159"
  AttacherType = Attacher::AttachEngine3D
  Height = 2
  Length = 6
  Placement = pos=(42.7226,14.4491,25) rot=(0,0,1;1.96349rad)
  Width = 8
FEATURE [Part::Box] Box152  label="Krychle152"
  AttacherType = Attacher::AttachEngine3D
  Height = 10
  Length = 6
  Placement = pos=(-3,47,40) rot=(0,0,1;0rad)
  Width = 6
FEATURE [Part::Compound] Compound316
  Links = -> [Box152,Box154,Box151,Box155,Box153,Box156]
  Placement = pos=(0,0,-18) rot=(0,0,1;0rad)
FEATURE [Part::Cut] Cut163
  Base = -> Cut161
  Tool = -> Compound316
FEATURE [Part::Cylinder] Cylinder722  label="Válec722"
  Angle = 360
  AttacherType = Attacher::AttachEngine3D
  Height = 100
  Placement = pos=(-38.8029,16.0727,0) rot=(0,0,-1;1.5708rad)
  Radius = 1.5
FEATURE [Part::Cylinder] Cylinder723  label="Válec723"
  Angle = 360
  AttacherType = Attacher::AttachEngine3D
  Height = 100
  Placement = pos=(-38.8029,16.0727,0) rot=(0,0,-1;1.5708rad)
  Radius = 1.5
FEATURE [Part::Cylinder] Cylinder724  label="Válec724"
  Angle = 360
  AttacherType = Attacher::AttachEngine3D
  Height = 100
  Placement = pos=(16.0727,-38.8029,0) rot=(0,0,1;0.785398rad)
  Radius = 1.5
FEATURE [Part::Cylinder] Cylinder725  label="Válec725"
  Angle = 360
  AttacherType = Attacher::AttachEngine3D
  Height = 100
  Placement = pos=(41.0044,-9.09046,0) rot=(0,0,1;1.74533rad)
  Radius = 1.5
FEATURE [Part::Cylinder] Cylinder726  label="Válec726"
  Angle = 360
  AttacherType = Attacher::AttachEngine3D
  Height = 100
  Placement = pos=(-41.0044,-9.09046,0) rot=(0,0,-1;0.959931rad)
  Radius = 1.5
FEATURE [Part::Box] Box163  label="Krychle163"
  AttacherType = Attacher::AttachEngine3D
  Height = 2
  Length = 6
  Placement = pos=(-44.5826,-6.81089,25) rot=(0,0,-1;1.35263rad)
  Width = 8
FEATURE [Part::Cylinder] Cylinder727  label="Válec727"
  Angle = 360
  AttacherType = Attacher::AttachEngine3D
  Height = 100
  Placement = pos=(16.0727,-38.8029,0) rot=(0,0,1;0.785398rad)
  Radius = 1.5
FEATURE [Part::Box] Box164  label="Krychle164"
  AttacherType = Attacher::AttachEngine3D
  Height = 2
  Length = 6
  Placement = pos=(-19.9924,-40.4265,25) rot=(0,0,-1;0.392699rad)
  Width = 8
FEATURE [Part::Cylinder] Cylinder728  label="Válec728"
  Angle = 360
  AttacherType = Attacher::AttachEngine3D
  Height = 100
  Placement = pos=(16.0727,38.8029,0) rot=(0,0,1;3.14159rad)
  Radius = 1.5
FEATURE [Part::Cylinder] Cylinder729  label="Válec729"
  Angle = 360
  AttacherType = Attacher::AttachEngine3D
  Height = 100
  Placement = pos=(-16.0727,-38.8029,0) rot=(0,0,1;0rad)
  Radius = 1.5
FEATURE [Part::Box] Box161  label="Krychle161"
  AttacherType = Attacher::AttachEngine3D
  Height = 2
  Length = 6
  Placement = pos=(-14.4491,42.7226,25) rot=(0,0,1;3.53429rad)
  Width = 8
FEATURE [Part::Cylinder] Cylinder730  label="Válec730"
  Angle = 360
  AttacherType = Attacher::AttachEngine3D
  Height = 100
  Placement = pos=(38.8029,16.0727,0) rot=(0,0,1;2.35619rad)
  Radius = 1.5
FEATURE [Part::Box] Box160  label="Krychle160"
  AttacherType = Attacher::AttachEngine3D
  Height = 2
  Length = 6
  Placement = pos=(19.9924,40.4265,25) rot=(0,0,1;2.74889rad)
  Width = 8
FEATURE [Part::Compound] Compound322
  Links = -> [Box157,Box158,Box159,Box160,Box161,Box162,Box163,Box164]
FEATURE [Part::Cylinder] Cylinder731  label="Válec731"
  Angle = 360
  AttacherType = Attacher::AttachEngine3D
  Height = 100
  Placement = pos=(-16.0727,38.8029,0) rot=(0,0,1;3.92699rad)
  Radius = 1.5
FEATURE [Part::Cylinder] Cylinder732  label="Válec732"
  Angle = 360
  AttacherType = Attacher::AttachEngine3D
  Height = 100
  Placement = pos=(-41.0044,-9.09046,0) rot=(0,0,-1;0.959931rad)
  Radius = 1.5
FEATURE [Part::Cylinder] Cylinder733  label="Válec733"
  Angle = 360
  AttacherType = Attacher::AttachEngine3D
  Height = 100
  Placement = pos=(16.0727,38.8029,0) rot=(0,0,1;3.14159rad)
  Radius = 1.5
FEATURE [Part::Compound] Compound702
  Links = -> [Cylinder727,Cylinder725,Cylinder730,Cylinder733,Cylinder731,Cylinder722,Cylinder732,Cylinder729]
FEATURE [Part::Cut] Cut322
  Base = -> Cut163
  Tool = -> Compound702
FEATURE [Part::Cylinder] Cylinder531  label="Válec531"
  Angle = 360
  AttacherType = Attacher::AttachEngine3D
  Height = 7
  Placement = pos=(39,-21,50) rot=(0,0,1;0rad)
  Radius = 3
FEATURE [Part::Cylinder] Cylinder533  label="Válec533"
  Angle = 360
  AttacherType = Attacher::AttachEngine3D
  Height = 7
  Placement = pos=(39,-21,50) rot=(0,0,1;0rad)
  Radius = 3
FEATURE [Part::Cylinder] Cylinder734  label="Válec734"
  Angle = 360
  AttacherType = Attacher::AttachEngine3D
  Height = 100
  Placement = pos=(38.8029,16.0727,0) rot=(0,0,1;2.35619rad)
  Radius = 1.5
FEATURE [Part::Cylinder] Cylinder735  label="Válec735"
  Angle = 360
  AttacherType = Attacher::AttachEngine3D
  Height = 100
  Placement = pos=(-16.0727,38.8029,0) rot=(0,0,1;3.92699rad)
  Radius = 1.5
FEATURE [Part::Cylinder] Cylinder532  label="Válec532"
  Angle = 360
  AttacherType = Attacher::AttachEngine3D
  Height = 7
  Placement = pos=(-39,-21,50) rot=(0,0,1;0rad)
  Radius = 3
FEATURE [Part::Compound] Compound706
  Links = -> [Cylinder532,Cylinder533]
  Placement = pos=(0,0,-25) rot=(0,0,1;0rad)
FEATURE [Part::Cylinder] Cylinder528  label="Válec528"
  Angle = 360
  AttacherType = Attacher::AttachEngine3D
  Height = 100
  Placement = pos=(-39,-21,0) rot=(0,0,1;0rad)
  Radius = 1.5
FEATURE [Part::Cylinder] Cylinder530  label="Válec530"
  Angle = 360
  AttacherType = Attacher::AttachEngine3D
  Height = 7
  Placement = pos=(-39,-21,50) rot=(0,0,1;0rad)
  Radius = 3
FEATURE [Part::Compound] Compound705
  Links = -> [Cylinder530,Cylinder531]
  Placement = pos=(0,0,-25) rot=(0,0,1;0rad)
FEATURE [Part::Cylinder] Cylinder736  label="Válec736"
  Angle = 360
  AttacherType = Attacher::AttachEngine3D
  Height = 100
  Placement = pos=(-16.0727,-38.8029,0) rot=(0,0,1;0rad)
  Radius = 1.5
FEATURE [Part::Cylinder] Cylinder529  label="Válec529"
  Angle = 360
  AttacherType = Attacher::AttachEngine3D
  Height = 100
  Placement = pos=(39,-21,0) rot=(0,0,1;0rad)
  Radius = 1.5
FEATURE [Part::Compound] Compound704
  Links = -> [Cylinder528,Cylinder529]
FEATURE [Part::Cylinder] Cylinder737  label="Válec737"
  Angle = 360
  AttacherType = Attacher::AttachEngine3D
  Height = 100
  Placement = pos=(41.0044,-9.09046,0) rot=(0,0,1;1.74533rad)
  Radius = 1.5
FEATURE [Part::Compound] Compound328
  Links = -> [Cylinder724,Cylinder737,Cylinder734,Cylinder728,Cylinder735,Cylinder723,Cylinder726,Cylinder736]
  Placement = pos=(0,0,20) rot=(0,0,1;0rad)
FEATURE [Part::Cut] Cut321
  Base = -> Cut164
  Tool = -> Compound328
FEATURE [Part::Cut] Cut323
  Base = -> Cut321
  Tool = -> Compound322
FEATURE [Part::Cut] Cut324
  Base = -> Cut322
  Tool = -> Compound705
FEATURE [Part::Cut] Cut176
  Base = -> Cut323
  Tool = -> Compound706
FEATURE [Part::Cut] Cut177
  Base = -> Cut176
  Tool = -> Compound704
FEATURE [Part::Compound] Compound703  label="bazovina-part-C_loziskovina"
  Links = -> [Cut324,Cut177]
FEATURE [Part::Cylinder] Cylinder738  label="Válec738"
  Angle = 360
  AttacherType = Attacher::AttachEngine3D
  Height = 100
  Placement = pos=(-16.0727,-38.8029,0) rot=(0,0,1;0rad)
  Radius = 1.5
FEATURE [Part::Cylinder] Cylinder739  label="Válec739"
  Angle = 360
  AttacherType = Attacher::AttachEngine3D
  Height = 100
  Placement = pos=(-38.8029,16.0727,0) rot=(0,0,-1;1.5708rad)
  Radius = 1.5
FEATURE [Part::Cylinder] Cylinder740  label="Válec740"
  Angle = 360
  AttacherType = Attacher::AttachEngine3D
  Height = 100
  Placement = pos=(41.0044,-9.09046,0) rot=(0,0,1;1.74533rad)
  Radius = 1.5
FEATURE [Part::Cylinder] Cylinder741  label="Válec741"
  Angle = 360
  AttacherType = Attacher::AttachEngine3D
  Height = 100
  Placement = pos=(38.8029,16.0727,0) rot=(0,0,1;2.35619rad)
  Radius = 1.5
FEATURE [Part::Cylinder] Cylinder742  label="Válec742"
  Angle = 360
  AttacherType = Attacher::AttachEngine3D
  Height = 100
  Placement = pos=(16.0727,-38.8029,0) rot=(0,0,1;0.785398rad)
  Radius = 1.5
FEATURE [Part::Cylinder] Cylinder743  label="Válec743"
  Angle = 360
  AttacherType = Attacher::AttachEngine3D
  Height = 100
  Placement = pos=(-16.0727,38.8029,0) rot=(0,0,1;3.92699rad)
  Radius = 1.5
FEATURE [Part::Cylinder] Cylinder744  label="Válec744"
  Angle = 360
  AttacherType = Attacher::AttachEngine3D
  Height = 100
  Placement = pos=(-41.0044,-9.09046,0) rot=(0,0,-1;0.959931rad)
  Radius = 1.5
FEATURE [Part::Cylinder] Cylinder745  label="Válec745"
  Angle = 360
  AttacherType = Attacher::AttachEngine3D
  Height = 100
  Placement = pos=(16.0727,38.8029,0) rot=(0,0,1;3.14159rad)
  Radius = 1.5
FEATURE [Part::Compound] Compound707
  Links = -> [Cylinder742,Cylinder740,Cylinder741,Cylinder745,Cylinder743,Cylinder739,Cylinder744,Cylinder738]
FEATURE [Part::Cylinder] Cylinder746  label="Válec746"
  Angle = 360
  AttacherType = Attacher::AttachEngine3D
  Height = 20
  Placement = pos=(-38.8029,16.0727,0) rot=(0,0,-1;1.5708rad)
  Radius = 8
FEATURE [Part::Cylinder] Cylinder747  label="Válec747"
  Angle = 360
  AttacherType = Attacher::AttachEngine3D
  Height = 20
  Placement = pos=(38.8029,16.0727,0) rot=(0,0,1;2.35619rad)
  Radius = 8
FEATURE [Part::Cylinder] Cylinder748  label="Válec748"
  Angle = 360
  AttacherType = Attacher::AttachEngine3D
  Height = 20
  Placement = pos=(-16.0727,-38.8029,0) rot=(0,0,1;0rad)
  Radius = 8
FEATURE [Part::Cylinder] Cylinder749  label="Válec749"
  Angle = 360
  AttacherType = Attacher::AttachEngine3D
  Height = 20
  Placement = pos=(41.0044,-9.09046,0) rot=(0,0,1;1.74533rad)
  Radius = 8
FEATURE [Part::Cylinder] Cylinder750  label="Válec750"
  Angle = 360
  AttacherType = Attacher::AttachEngine3D
  Height = 20
  Placement = pos=(-41.0044,-9.09046,0) rot=(0,0,-1;0.959931rad)
  Radius = 8
FEATURE [Part::Cylinder] Cylinder751  label="Válec751"
  Angle = 360
  AttacherType = Attacher::AttachEngine3D
  Height = 20
  Placement = pos=(16.0727,38.8029,0) rot=(0,0,1;3.14159rad)
  Radius = 8
FEATURE [Part::Cylinder] Cylinder752  label="Válec752"
  Angle = 360
  AttacherType = Attacher::AttachEngine3D
  Height = 20
  Placement = pos=(16.0727,-38.8029,0) rot=(0,0,1;0.785398rad)
  Radius = 8
FEATURE [Part::Cylinder] Cylinder753  label="Válec753"
  Angle = 360
  AttacherType = Attacher::AttachEngine3D
  Height = 20
  Placement = pos=(-16.0727,38.8029,0) rot=(0,0,1;3.92699rad)
  Radius = 8
FEATURE [Part::Compound] Compound708
  Links = -> [Cylinder752,Cylinder749,Cylinder747,Cylinder751,Cylinder753,Cylinder746,Cylinder750,Cylinder748]
  Placement = pos=(0,0,56) rot=(0,0,1;0rad)
FEATURE [Part::FeaturePython] Tube079  # WARN: FeaturePython — macro-defined, semantics opaque (R4)
  AttacherType = Attacher::AttachEngine3D
  Height = 1
  InnerRadius = 38
  OuterRadius = 58
  Placement = pos=(0,0,42) rot=(0,0,1;0rad)
FEATURE [Part::Cylinder] Cylinder754  label="Válec754"
  Angle = 360
  AttacherType = Attacher::AttachEngine3D
  Height = 100
  Placement = pos=(-38.8029,16.0727,0) rot=(0,0,-1;1.5708rad)
  Radius = 1.5
FEATURE [Part::Cylinder] Cylinder755  label="Válec755"
  Angle = 360
  AttacherType = Attacher::AttachEngine3D
  Height = 100
  Placement = pos=(38.8029,16.0727,0) rot=(0,0,1;2.35619rad)
  Radius = 1.5
FEATURE [Part::Cylinder] Cylinder756  label="Válec756"
  Angle = 360
  AttacherType = Attacher::AttachEngine3D
  Height = 100
  Placement = pos=(-16.0727,-38.8029,0) rot=(0,0,1;0rad)
  Radius = 1.5
FEATURE [Part::Cylinder] Cylinder757  label="Válec757"
  Angle = 360
  AttacherType = Attacher::AttachEngine3D
  Height = 100
  Placement = pos=(41.0044,-9.09046,0) rot=(0,0,1;1.74533rad)
  Radius = 1.5
FEATURE [Part::Cylinder] Cylinder758  label="Válec758"
  Angle = 360
  AttacherType = Attacher::AttachEngine3D
  Height = 100
  Placement = pos=(-41.0044,-9.09046,0) rot=(0,0,-1;0.959931rad)
  Radius = 1.5
FEATURE [Part::Cylinder] Cylinder759  label="Válec759"
  Angle = 360
  AttacherType = Attacher::AttachEngine3D
  Height = 100
  Placement = pos=(16.0727,38.8029,0) rot=(0,0,1;3.14159rad)
  Radius = 1.5
FEATURE [Part::Cylinder] Cylinder760  label="Válec760"
  Angle = 360
  AttacherType = Attacher::AttachEngine3D
  Height = 100
  Placement = pos=(16.0727,-38.8029,0) rot=(0,0,1;0.785398rad)
  Radius = 1.5
FEATURE [Part::Cylinder] Cylinder761  label="Válec761"
  Angle = 360
  AttacherType = Attacher::AttachEngine3D
  Height = 100
  Placement = pos=(-16.0727,38.8029,0) rot=(0,0,1;3.92699rad)
  Radius = 1.5
FEATURE [Part::Compound] Compound709
  Links = -> [Cylinder760,Cylinder757,Cylinder755,Cylinder759,Cylinder761,Cylinder754,Cylinder758,Cylinder756]
FEATURE [Part::Cylinder] Cylinder762  label="Válec762"
  Angle = 360
  AttacherType = Attacher::AttachEngine3D
  Height = 20
  Placement = pos=(-16.0727,38.8029,0) rot=(0,0,1;3.92699rad)
  Radius = 8
FEATURE [Part::Cylinder] Cylinder763  label="Válec763"
  Angle = 360
  AttacherType = Attacher::AttachEngine3D
  Height = 20
  Placement = pos=(-16.0727,-38.8029,0) rot=(0,0,1;0rad)
  Radius = 8
FEATURE [Part::Cylinder] Cylinder764  label="Válec764"
  Angle = 360
  AttacherType = Attacher::AttachEngine3D
  Height = 20
  Placement = pos=(-41.0044,-9.09046,0) rot=(0,0,-1;0.959931rad)
  Radius = 8
FEATURE [Part::Cylinder] Cylinder765  label="Válec765"
  Angle = 360
  AttacherType = Attacher::AttachEngine3D
  Height = 20
  Placement = pos=(38.8029,16.0727,0) rot=(0,0,1;2.35619rad)
  Radius = 8
FEATURE [Part::Cylinder] Cylinder766  label="Válec766"
  Angle = 360
  AttacherType = Attacher::AttachEngine3D
  Height = 20
  Placement = pos=(41.0044,-9.09046,0) rot=(0,0,1;1.74533rad)
  Radius = 8
FEATURE [Part::Cylinder] Cylinder767  label="Válec767"
  Angle = 360
  AttacherType = Attacher::AttachEngine3D
  Height = 20
  Placement = pos=(16.0727,38.8029,0) rot=(0,0,1;3.14159rad)
  Radius = 8
FEATURE [Part::Cylinder] Cylinder768  label="Válec768"
  Angle = 360
  AttacherType = Attacher::AttachEngine3D
  Height = 20
  Placement = pos=(16.0727,-38.8029,0) rot=(0,0,1;0.785398rad)
  Radius = 8
FEATURE [Part::Cylinder] Cylinder769  label="Válec769"
  Angle = 360
  AttacherType = Attacher::AttachEngine3D
  Height = 20
  Placement = pos=(-38.8029,16.0727,0) rot=(0,0,-1;1.5708rad)
  Radius = 8
FEATURE [Part::Compound] Compound710
  Links = -> [Cylinder768,Cylinder766,Cylinder765,Cylinder767,Cylinder762,Cylinder769,Cylinder764,Cylinder763]
  Placement = pos=(0,0,56) rot=(0,0,1;0rad)
FEATURE [Part::Cut] Cut325  label="bazovina_part-F_washer"
  Base = -> Tube079
  Tool = -> Compound709
FEATURE [Part::Cylinder] Cylinder770  label="Válec770"
  Angle = 360
  AttacherType = Attacher::AttachEngine3D
  Height = 20
  Placement = pos=(0,0,91) rot=(0,0,1;0rad)
  Radius = 38
FEATURE [Part::Cylinder] Cylinder771  label="Válec771"
  Angle = 360
  AttacherType = Attacher::AttachEngine3D
  Height = 20
  Placement = pos=(0,0,91) rot=(0,0,1;0rad)
  Radius = 38
FEATURE [Part::Cylinder] Cylinder772  label="Válec772"
  Angle = 360
  AttacherType = Attacher::AttachEngine3D
  Height = 100
  Placement = pos=(38.8029,-16.0727,0) rot=(0,0,1;1.5708rad)
  Radius = 1.5
FEATURE [Part::FeaturePython] wormgear024  # WARN: FeaturePython — macro-defined, semantics opaque (R4)
  AttacherType = Attacher::AttachEngine3D
  Placement = pos=(0,0,95) rot=(0,0,1;0.032289rad)
  beta = 33.6901
  clearance = 0.25
  diameter = 120
  head = 0
  height = 5
  module = 1
  pressure_angle = 20
  reverse_pitch = false
  teeth = 80
  version = 0.0.3
FEATURE [Part::Cut] Cut326
  Base = -> wormgear024
  Placement = pos=(0,0,-63) rot=(0,0,1;0rad)
  Tool = -> Cylinder771
FEATURE [Part::FeaturePython] wormgear025  # WARN: FeaturePython — macro-defined, semantics opaque (R4)
  AttacherType = Attacher::AttachEngine3D
  Placement = pos=(0,0,100) rot=(0,0,1;0rad)
  beta = 33.6901
  clearance = 0.25
  diameter = 120
  head = 0
  height = 5
  module = 1
  pressure_angle = 20
  reverse_pitch = true
  teeth = 80
  version = 0.0.3
FEATURE [Part::Cut] Cut327
  Base = -> wormgear025
  Placement = pos=(0,0,-63) rot=(0,0,1;0rad)
  Tool = -> Cylinder770
FEATURE [Part::Cylinder] Cylinder773  label="Válec773"
  Angle = 360
  AttacherType = Attacher::AttachEngine3D
  Height = 100
  Placement = pos=(-16.0727,38.8029,0) rot=(0,0,1;3.92699rad)
  Radius = 1.5
FEATURE [Part::Cylinder] Cylinder774  label="Válec774"
  Angle = 360
  AttacherType = Attacher::AttachEngine3D
  Height = 100
  Placement = pos=(-38.8029,16.0727,0) rot=(0,0,-1;1.5708rad)
  Radius = 1.5
FEATURE [Part::Cylinder] Cylinder775  label="Válec775"
  Angle = 360
  AttacherType = Attacher::AttachEngine3D
  Height = 100
  Placement = pos=(-16.0727,38.8029,0) rot=(0,0,1;3.92699rad)
  Radius = 1.5
FEATURE [Part::Cylinder] Cylinder776  label="Válec776"
  Angle = 360
  AttacherType = Attacher::AttachEngine3D
  Height = 100
  Placement = pos=(9.09046,41.0044,0) rot=(0,0,1;3.31613rad)
  Radius = 1.5
FEATURE [Part::Cylinder] Cylinder777  label="Válec777"
  Angle = 360
  AttacherType = Attacher::AttachEngine3D
  Height = 100
  Placement = pos=(-38.8029,-16.0727,0) rot=(0,0,-1;0.785398rad)
  Radius = 1.5
FEATURE [Part::Cylinder] Cylinder778  label="Válec778"
  Angle = 360
  AttacherType = Attacher::AttachEngine3D
  Height = 100
  Placement = pos=(-38.8029,-16.0727,0) rot=(0,0,-1;0.785398rad)
  Radius = 1.5
FEATURE [Part::Cylinder] Cylinder779  label="Válec779"
  Angle = 360
  AttacherType = Attacher::AttachEngine3D
  Height = 100
  Placement = pos=(9.09046,41.0044,0) rot=(0,0,1;3.31613rad)
  Radius = 1.5
FEATURE [Part::Cylinder] Cylinder780  label="Válec780"
  Angle = 360
  AttacherType = Attacher::AttachEngine3D
  Height = 100
  Placement = pos=(38.8029,16.0727,0) rot=(0,0,1;2.35619rad)
  Radius = 1.5
FEATURE [Part::Cylinder] Cylinder781  label="Válec781"
  Angle = 360
  AttacherType = Attacher::AttachEngine3D
  Height = 100
  Placement = pos=(38.8029,-16.0727,0) rot=(0,0,1;1.5708rad)
  Radius = 1.5
FEATURE [Part::Cylinder] Cylinder782  label="Válec782"
  Angle = 360
  AttacherType = Attacher::AttachEngine3D
  Height = 100
  Placement = pos=(38.8029,16.0727,0) rot=(0,0,1;2.35619rad)
  Radius = 1.5
FEATURE [Part::Cylinder] Cylinder783  label="Válec783"
  Angle = 360
  AttacherType = Attacher::AttachEngine3D
  Height = 100
  Placement = pos=(-16.0727,-38.8029,0) rot=(0,0,1;0rad)
  Radius = 1.5
FEATURE [Part::Cylinder] Cylinder784  label="Válec784"
  Angle = 360
  AttacherType = Attacher::AttachEngine3D
  Height = 100
  Placement = pos=(-16.0727,-38.8029,0) rot=(0,0,1;0rad)
  Radius = 1.5
FEATURE [Part::Cylinder] Cylinder785  label="Válec785"
  Angle = 360
  AttacherType = Attacher::AttachEngine3D
  Height = 100
  Placement = pos=(9.09046,-41.0044,0) rot=(0,0,1;0.610865rad)
  Radius = 1.5
FEATURE [Part::Compound] Compound711
  Links = -> [Cylinder785,Cylinder772,Cylinder782,Cylinder776,Cylinder775,Cylinder774,Cylinder777,Cylinder783]
FEATURE [Part::Cut] Cut329
  Base = -> Cut326
  Tool = -> Compound711
FEATURE [Part::Cylinder] Cylinder786  label="Válec786"
  Angle = 360
  AttacherType = Attacher::AttachEngine3D
  Height = 100
  Placement = pos=(9.09046,-41.0044,0) rot=(0,0,1;0.610865rad)
  Radius = 1.5
FEATURE [Part::Cylinder] Cylinder787  label="Válec787"
  Angle = 360
  AttacherType = Attacher::AttachEngine3D
  Height = 100
  Placement = pos=(-38.8029,16.0727,0) rot=(0,0,-1;1.5708rad)
  Radius = 1.5
FEATURE [Part::Compound] Compound712
  Links = -> [Cylinder786,Cylinder781,Cylinder780,Cylinder779,Cylinder773,Cylinder787,Cylinder778,Cylinder784]
FEATURE [Part::Cut] Cut328
  Base = -> Cut327
  Tool = -> Compound712
FEATURE [Part::Compound] Compound713  label="bazovina-part-D_ozubo2"
  Links = -> [Cut328,Cut329]
FEATURE [Part::Cylinder] Cylinder788  label="Válec788"
  Angle = 360
  AttacherType = Attacher::AttachEngine3D
  Height = 100
  Placement = pos=(-16.0727,-38.8029,0) rot=(0,0,1;0rad)
  Radius = 1.5
FEATURE [Part::Cylinder] Cylinder789  label="Válec789"
  Angle = 360
  AttacherType = Attacher::AttachEngine3D
  Height = 100
  Placement = pos=(41.0044,-9.09046,0) rot=(0,0,1;1.74533rad)
  Radius = 1.5
FEATURE [Part::Cylinder] Cylinder790  label="Válec790"
  Angle = 360
  AttacherType = Attacher::AttachEngine3D
  Height = 100
  Placement = pos=(-38.8029,16.0727,0) rot=(0,0,-1;1.5708rad)
  Radius = 1.5
FEATURE [Part::Cylinder] Cylinder791  label="Válec791"
  Angle = 360
  AttacherType = Attacher::AttachEngine3D
  Height = 100
  Placement = pos=(38.8029,16.0727,0) rot=(0,0,1;2.35619rad)
  Radius = 1.5
FEATURE [Part::FeaturePython] Tube080  # WARN: FeaturePython — macro-defined, semantics opaque (R4)
  AttacherType = Attacher::AttachEngine3D
  Height = 1
  InnerRadius = 38
  OuterRadius = 58
  Placement = pos=(0,0,42) rot=(0,0,1;0rad)
FEATURE [Part::Cylinder] Cylinder792  label="Válec792"
  Angle = 360
  AttacherType = Attacher::AttachEngine3D
  Height = 100
  Placement = pos=(16.0727,38.8029,0) rot=(0,0,1;3.14159rad)
  Radius = 1.5
FEATURE [Part::Cylinder] Cylinder793  label="Válec793"
  Angle = 360
  AttacherType = Attacher::AttachEngine3D
  Height = 100
  Placement = pos=(-41.0044,-9.09046,0) rot=(0,0,-1;0.959931rad)
  Radius = 1.5
FEATURE [Part::Cylinder] Cylinder794  label="Válec794"
  Angle = 360
  AttacherType = Attacher::AttachEngine3D
  Height = 100
  Placement = pos=(16.0727,-38.8029,0) rot=(0,0,1;0.785398rad)
  Radius = 1.5
FEATURE [Part::Cylinder] Cylinder795  label="Válec795"
  Angle = 360
  AttacherType = Attacher::AttachEngine3D
  Height = 100
  Placement = pos=(-16.0727,38.8029,0) rot=(0,0,1;3.92699rad)
  Radius = 1.5
FEATURE [Part::Compound] Compound714
  Links = -> [Cylinder794,Cylinder789,Cylinder791,Cylinder792,Cylinder795,Cylinder790,Cylinder793,Cylinder788]
FEATURE [Part::Cut] Cut330  label="bazovina_part-F_washer001"
  Base = -> Tube080
  Placement = pos=(0,0,0) rot=(0,0,1;1.5708rad)
  Tool = -> Compound714
FEATURE [Part::Compound] Compound715  label="bazovina_part-D_ozubo-washer"
  Links = -> [Compound713,Cut330]
  Placement = pos=(0,0,0) rot=(0,0,-1;1.5708rad)
FEATURE [Part::FeaturePython] Tube081  # WARN: FeaturePython — macro-defined, semantics opaque (R4)
  AttacherType = Attacher::AttachEngine3D
  Height = 8
  InnerRadius = 30
  OuterRadius = 38.75
  Placement = pos=(0,0,58) rot=(0,0,1;0rad)
FEATURE [Part::FeaturePython] Tube082  # WARN: FeaturePython — macro-defined, semantics opaque (R4)
  AttacherType = Attacher::AttachEngine3D
  Height = 8
  InnerRadius = 30
  OuterRadius = 58
  Placement = pos=(0,0,52) rot=(0,0,1;0rad)
FEATURE [Part::FeaturePython] Tube083  # WARN: FeaturePython — macro-defined, semantics opaque (R4)
  AttacherType = Attacher::AttachEngine3D
  Height = 3
  InnerRadius = 54
  OuterRadius = 61
  Placement = pos=(0,0,52) rot=(0,0,1;0rad)
FEATURE [Part::Chamfer] Chamfer003
  Base = -> Tube083
  Edges = 1 edges r=1: [Edge3]
FEATURE [Part::Cylinder] Cylinder796  label="Válec796"
  Angle = 360
  AttacherType = Attacher::AttachEngine3D
  Height = 100
  Placement = pos=(-38.8029,16.0727,0) rot=(0,0,-1;1.5708rad)
  Radius = 1.5
FEATURE [Part::Cylinder] Cylinder797  label="Válec797"
  Angle = 360
  AttacherType = Attacher::AttachEngine3D
  Height = 100
  Placement = pos=(38.8029,16.0727,0) rot=(0,0,1;2.35619rad)
  Radius = 1.5
FEATURE [Part::Cylinder] Cylinder798  label="Válec798"
  Angle = 360
  AttacherType = Attacher::AttachEngine3D
  Height = 100
  Placement = pos=(-16.0727,-38.8029,0) rot=(0,0,1;0rad)
  Radius = 1.5
FEATURE [Part::Cylinder] Cylinder799  label="Válec799"
  Angle = 360
  AttacherType = Attacher::AttachEngine3D
  Height = 100
  Placement = pos=(41.0044,-9.09046,0) rot=(0,0,1;1.74533rad)
  Radius = 1.5
FEATURE [Part::Cylinder] Cylinder800  label="Válec800"
  Angle = 360
  AttacherType = Attacher::AttachEngine3D
  Height = 100
  Placement = pos=(-41.0044,-9.09046,0) rot=(0,0,-1;0.959931rad)
  Radius = 1.5
FEATURE [Part::Cylinder] Cylinder801  label="Válec801"
  Angle = 360
  AttacherType = Attacher::AttachEngine3D
  Height = 100
  Placement = pos=(16.0727,38.8029,0) rot=(0,0,1;3.14159rad)
  Radius = 1.5
FEATURE [Part::Cylinder] Cylinder802  label="Válec802"
  Angle = 360
  AttacherType = Attacher::AttachEngine3D
  Height = 100
  Placement = pos=(16.0727,-38.8029,0) rot=(0,0,1;0.785398rad)
  Radius = 1.5
FEATURE [Part::Cylinder] Cylinder803  label="Válec803"
  Angle = 360
  AttacherType = Attacher::AttachEngine3D
  Height = 100
  Placement = pos=(-16.0727,38.8029,0) rot=(0,0,1;3.92699rad)
  Radius = 1.5
FEATURE [Part::Compound] Compound716
  Links = -> [Cylinder802,Cylinder799,Cylinder797,Cylinder801,Cylinder803,Cylinder796,Cylinder800,Cylinder798]
FEATURE [Part::Cut] Cut331
  Base = -> Tube081
  Tool = -> Compound708
FEATURE [Part::Chamfer] Chamfer004
  Base = -> Cut331
  Edges = 9 edges r=1: [Edge4,Edge5,Edge26,Edge28,Edge30,Edge32,Edge34,Edge36,Edge38]
FEATURE [Part::Cut] Cut332
  Base = -> Tube082
  Tool = -> Compound710
FEATURE [Part::Cut] Cut333
  Base = -> Cut332
  Tool = -> Compound716
FEATURE [Part::Compound] Compound717  label="bazovina_part-F_pedestal-axial-B"
  Links = -> [Chamfer003,Chamfer004,Cut333]
FEATURE [Part::Box] Box307  label="Krychle307"
  AttacherType = Attacher::AttachEngine3D
  Height = 7
  Length = 60
  Placement = pos=(0,0,-22) rot=(0,0,-1;0.349066rad)
  Width = 60
FEATURE [Part::Box] Box308  label="Krychle308"
  AttacherType = Attacher::AttachEngine3D
  Height = 7
  Length = 60
  Placement = pos=(-56.3816,-20.5212,-22) rot=(0,0,1;0.349066rad)
  Width = 60
FEATURE [Part::Compound] Compound718
  Links = -> [Box307,Box308]
FEATURE [Part::Box] Box309  label="Krychle309"
  AttacherType = Attacher::AttachEngine3D
  Height = 7
  Length = 120
  Placement = pos=(-60,-60,-22) rot=(0,0,-1;0rad)
  Width = 60
FEATURE [Part::FeaturePython] Tube084  # WARN: FeaturePython — macro-defined, semantics opaque (R4)
  AttacherType = Attacher::AttachEngine3D
  Height = 7
  InnerRadius = 53
  OuterRadius = 54.4
  Placement = pos=(0,0,-22) rot=(0,0,1;0rad)
FEATURE [Part::FeaturePython] Tube085  # WARN: FeaturePython — macro-defined, semantics opaque (R4)
  AttacherType = Attacher::AttachEngine3D
  Height = 7
  InnerRadius = 53
  OuterRadius = 54.4
  Placement = pos=(0,0,-22) rot=(0,0,1;0rad)
FEATURE [Part::Cut] Cut334
  Base = -> Tube085
  Tool = -> Box309
FEATURE [Part::Cut] Cut336
  Base = -> Cut334
  Placement = pos=(0,0,-7) rot=(0,0,1;0rad)
  Tool = -> Compound718
FEATURE [Part::Box] Box310  label="Krychle310"
  AttacherType = Attacher::AttachEngine3D
  Height = 7
  Length = 120
  Placement = pos=(-60,-60,-22) rot=(0,0,-1;0rad)
  Width = 60
FEATURE [Part::Cut] Cut337
  Base = -> Tube084
  Tool = -> Box310
FEATURE [Part::Box] Box311  label="Krychle311"
  AttacherType = Attacher::AttachEngine3D
  Height = 7
  Length = 60
  Placement = pos=(-59.9909,-1.04714,-22) rot=(0,0,1;0.017453rad)
  Width = 60
FEATURE [Part::Box] Box312  label="Krychle312"
  AttacherType = Attacher::AttachEngine3D
  Height = 7
  Length = 60
  Placement = pos=(0,0,-22) rot=(0,0,-1;0.034907rad)
  Width = 60
FEATURE [Part::Compound] Compound719
  Links = -> [Box312,Box311]
FEATURE [Part::Cut] Cut338
  Base = -> Cut337
  Placement = pos=(0,0,-7) rot=(0,0,1;0rad)
  Tool = -> Compound719
FEATURE [Part::Cut] Cut335
  Base = -> Cut336
  Placement = pos=(0,0,74) rot=(0,0,1;3.92699rad)
  Tool = -> Cut338
FEATURE [Part::Box] Box313  label="Krychle313"
  AttacherType = Attacher::AttachEngine3D
  Height = 7
  Length = 1.4
  Placement = pos=(0,0,-22) rot=(0,0,1;0.047124rad)
  Width = 60
FEATURE [Part::Cylinder] Cylinder804  label="Válec804"
  Angle = 360
  AttacherType = Attacher::AttachEngine3D
  Height = 7
  Placement = pos=(0,0,-22) rot=(0,0,1;0rad)
  Radius = 52
FEATURE [Part::Box] Box314  label="Krychle314"
  AttacherType = Attacher::AttachEngine3D
  Height = 7
  Length = 1.4
  Placement = pos=(0,0,-22) rot=(0,0,-1;0.034907rad)
  Width = 60
FEATURE [Part::Compound] Compound720
  Links = -> [Box314,Box313]
FEATURE [Part::Cut] Cut339
  Base = -> Compound720
  Placement = pos=(0,0,67) rot=(0,0,1;3.92524rad)
  Tool = -> Cylinder804
FEATURE [Part::FeaturePython] Tube086  # WARN: FeaturePython — macro-defined, semantics opaque (R4)
  AttacherType = Attacher::AttachEngine3D
  Height = 3
  InnerRadius = 54
  OuterRadius = 61
  Placement = pos=(0,0,42) rot=(0,0,1;0rad)
FEATURE [Part::Chamfer] Chamfer005
  Base = -> Tube086
  Edges = 1 edges r=1: [Edge1]
FEATURE [Part::FeaturePython] Tube087  # WARN: FeaturePython — macro-defined, semantics opaque (R4)
  AttacherType = Attacher::AttachEngine3D
  Height = 10
  InnerRadius = 30
  OuterRadius = 57
  Placement = pos=(0,0,42) rot=(0,0,1;0rad)
FEATURE [Part::Cylinder] Cylinder805  label="Válec805"
  Angle = 360
  AttacherType = Attacher::AttachEngine3D
  Height = 100
  Placement = pos=(-38.8029,16.0727,0) rot=(0,0,-1;1.5708rad)
  Radius = 1.5
FEATURE [Part::Cylinder] Cylinder806  label="Válec806"
  Angle = 360
  AttacherType = Attacher::AttachEngine3D
  Height = 100
  Placement = pos=(38.8029,16.0727,0) rot=(0,0,1;2.35619rad)
  Radius = 1.5
FEATURE [Part::Cylinder] Cylinder807  label="Válec807"
  Angle = 360
  AttacherType = Attacher::AttachEngine3D
  Height = 100
  Placement = pos=(-16.0727,-38.8029,0) rot=(0,0,1;0rad)
  Radius = 1.5
FEATURE [Part::Cylinder] Cylinder808  label="Válec808"
  Angle = 360
  AttacherType = Attacher::AttachEngine3D
  Height = 100
  Placement = pos=(41.0044,-9.09046,0) rot=(0,0,1;1.74533rad)
  Radius = 1.5
FEATURE [Part::Cylinder] Cylinder809  label="Válec809"
  Angle = 360
  AttacherType = Attacher::AttachEngine3D
  Height = 100
  Placement = pos=(-41.0044,-9.09046,0) rot=(0,0,-1;0.959931rad)
  Radius = 1.5
FEATURE [Part::Cylinder] Cylinder810  label="Válec810"
  Angle = 360
  AttacherType = Attacher::AttachEngine3D
  Height = 100
  Placement = pos=(16.0727,38.8029,0) rot=(0,0,1;3.14159rad)
  Radius = 1.5
FEATURE [Part::Cylinder] Cylinder811  label="Válec811"
  Angle = 360
  AttacherType = Attacher::AttachEngine3D
  Height = 100
  Placement = pos=(16.0727,-38.8029,0) rot=(0,0,1;0.785398rad)
  Radius = 1.5
FEATURE [Part::Cylinder] Cylinder812  label="Válec812"
  Angle = 360
  AttacherType = Attacher::AttachEngine3D
  Height = 100
  Placement = pos=(-16.0727,38.8029,0) rot=(0,0,1;3.92699rad)
  Radius = 1.5
FEATURE [Part::Compound] Compound721
  Links = -> [Cylinder811,Cylinder808,Cylinder806,Cylinder810,Cylinder812,Cylinder805,Cylinder809,Cylinder807]
FEATURE [Part::Cut] Cut340
  Base = -> Tube087
  Tool = -> Compound721
FEATURE [Part::Cut] Cut341
  Base = -> Cut340
  Tool = -> Cut339
FEATURE [Part::Cut] Cut342
  Base = -> Cut341
  Tool = -> Cut335
FEATURE [Part::Compound] Compound722  label="bazovina_part-F_pedestal-axial-A-belt"
  Links = -> [Chamfer005,Cut342]
FEATURE [Mesh::Feature] Mesh001  label="bazovina_part-F_pedestal-axial-B (Meshed)"
FEATURE [Mesh::Feature] Mesh002  label="bazovina_part-F_washer (Meshed)"
FEATURE [Mesh::Feature] Mesh  label="bazovina_part-F_pedestal-axial-A-belt (Meshed)"
FEATURE [Mesh::Feature] Mesh003  label="bazovina_part-F_pedestal-axial-B (Meshed)001"
